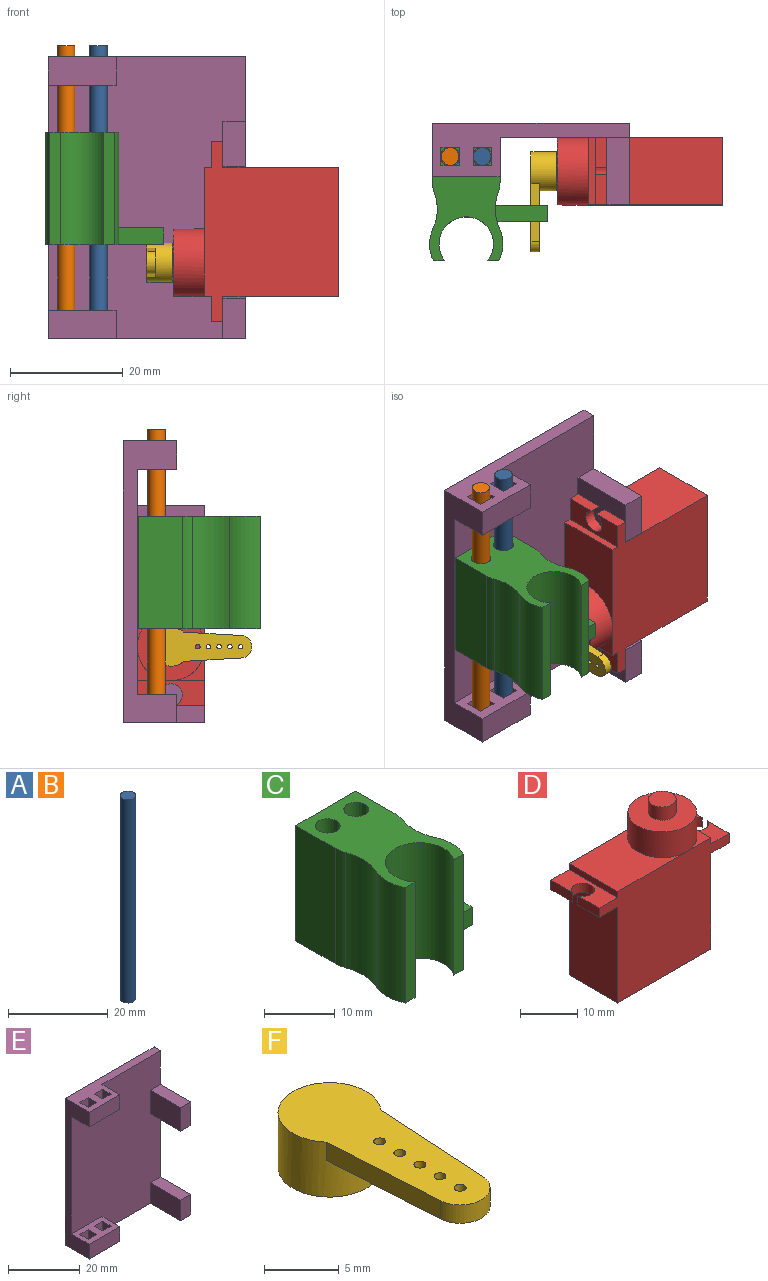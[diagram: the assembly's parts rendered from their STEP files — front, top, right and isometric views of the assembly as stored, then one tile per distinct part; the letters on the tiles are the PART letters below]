
ASSEMBLY  parts=6 mates=5
PART A: 3 faces, bbox 3.1x3.1x50 mm
  f0: cylinder r=1.55mm len=50mm, axis (0,0,-1), area 486.9mm2, adj f1,f2
  f1: plane 3.1x3.1mm, normal (0,0,1), area 7.5mm2, adj f0
  f2: plane 3.1x3.1mm, normal (0,0,-1), area 7.5mm2, adj f0
PART B: same geometry as A
PART C: 20 faces, bbox 21x21.7x20 mm
  f0: cylinder r=6.5mm len=20mm, axis (0,0,-1), area 116.8mm2, adj f1,f12,f14,f15
  f1: plane 20x1.94mm, normal (0,-1,0), area 38.8mm2, adj f0,f2,f14,f15
  f2: cylinder r=4.85mm len=20mm, axis (0,0,-1), area 431.5mm2, adj f1,f3,f14,f15
  f3: plane 20x1.94mm, normal (0,-1,0), area 38.8mm2, adj f2,f4,f14,f15
  f4: cylinder r=6.5mm len=20mm, axis (0,0,-1), area 116.8mm2, adj f3,f5,f14,f15
  f5: cylinder r=8.5mm len=20mm, axis (0,0,-1), area 124.3mm2, adj f4,f6,f14,f15,f16,f18,f19
  f6: cylinder r=5mm len=20mm, axis (0,0,-1), area 35.7mm2, adj f5,f7,f14,f15
  f7: plane 20x7.86mm, normal (1,0,0), area 157.2mm2, adj f6,f8,f14,f15
  f8: plane 20x12mm, normal (0,1,0), area 240mm2, adj f7,f9,f14,f15
  f9: plane 20x7.86mm, normal (-1,0,0), area 157.2mm2, adj f8,f10,f14,f15
  f10: cylinder r=5mm len=20mm, axis (0,0,-1), area 35.7mm2, adj f9,f12,f14,f15
  f11: cylinder r=1.75mm len=20mm, axis (0,0,-1), area 219.9mm2, adj f14,f15
  f12: cylinder r=8.5mm len=20mm, axis (0,0,-1), area 133.3mm2, adj f0,f10,f14,f15
  f13: cylinder r=1.75mm len=20mm, axis (0,0,-1), area 219.9mm2, adj f14,f15
  f14: plane 21.74x13mm, normal (0,0,1), area 172.7mm2, adj f0,f1,f2,f3,f4,f5,f6,f7
  f15: plane 21.74x21mm, normal (0,0,-1), area 200.5mm2, adj f0,f1,f2,f3,f4,f5,f6,f7
  f16: plane 9.05x3mm, normal (0,-1,0), area 27.1mm2, adj f5,f15,f17,f18
  f17: plane 3x3mm, normal (1,0,0), area 9mm2, adj f15,f16,f18,f19
  f18: plane 9.35x3mm, normal (0,0,1), area 27.8mm2, adj f5,f16,f17,f19
  f19: plane 9.32x3mm, normal (0,1,0), area 27.9mm2, adj f5,f15,f17,f18
PART D: 24 faces, bbox 32x12x32.1 mm
  f0: plane 6x6mm, normal (0,0,1), area 7.7mm2, adj f3,f4,f20
  f1: plane 17x12mm, normal (0,0,1), area 147.5mm2, adj f2,f4,f6,f20
  f2: plane 12x1.3mm, normal (-1,0,0), area 15.6mm2, adj f1,f4,f6,f18
  f3: plane 12x1.3mm, normal (1,0,0), area 15.6mm2, adj f0,f4,f6,f9,f13
  f4: plane 32x23.8mm, normal (0,-1,0), area 565.4mm2, adj f0,f1,f2,f3,f5,f7,f8,f10
  f5: plane 20.5x12mm, normal (1,0,0), area 246mm2, adj f4,f6,f8,f14
  f6: plane 32x23.8mm, normal (0,1,0), area 565.4mm2, adj f1,f2,f3,f5,f7,f8,f9,f12
  f7: plane 20.5x12mm, normal (-1,0,0), area 246mm2, adj f4,f6,f8,f19
  f8: plane 23x12mm, normal (0,0,-1), area 276mm2, adj f4,f5,f6,f7
  f9: plane 6x6mm, normal (0,0,1), area 7.7mm2, adj f3,f6,f20
  f10: plane 5.38x2mm, normal (1,0,0), area 10.8mm2, adj f4,f11,f13,f14
  f11: cylinder r=2mm len=4mm, axis (0,0,-1), area 22.6mm2, adj f10,f12,f13,f14
  f12: plane 5.38x2mm, normal (1,0,0), area 10.8mm2, adj f6,f11,f13,f14
  f13: plane 12x4.5mm, normal (0,0,1), area 41.5mm2, adj f3,f4,f6,f10,f11,f12
  f14: plane 12x4.5mm, normal (0,0,-1), area 41.5mm2, adj f4,f5,f6,f10,f11,f12
  f15: plane 5.38x2mm, normal (-1,0,0), area 10.8mm2, adj f6,f16,f18,f19
  f16: cylinder r=2mm len=4mm, axis (0,0,-1), area 22.6mm2, adj f15,f17,f18,f19
  f17: plane 5.38x2mm, normal (-1,0,0), area 10.8mm2, adj f4,f16,f18,f19
  f18: plane 12x4.5mm, normal (0,0,1), area 41.5mm2, adj f2,f4,f6,f15,f16,f17
  f19: plane 12x4.5mm, normal (0,0,-1), area 41.5mm2, adj f4,f6,f7,f15,f16,f17
  f20: cylinder r=6mm len=12mm, axis (0,0,-1), area 207.3mm2, adj f0,f1,f9,f21
  f21: plane 12x12mm, normal (0,0,1), area 94.6mm2, adj f20,f22
  f22: cylinder r=2.43mm len=4.85mm, axis (0,0,-1), area 42.7mm2, adj f21,f23
  f23: plane 4.85x4.85mm, normal (0,0,1), area 18.5mm2, adj f22
PART E: 37 faces, bbox 35x14.5x50 mm
  f0: plane 50x35mm, normal (0,-1,0), area 1570mm2, adj f7,f8,f9,f10,f13,f22,f25,f27
  f1: plane 3.3x3mm, normal (0,-1,0), area 9.9mm2, adj f2,f4,f27,f29
  f2: plane 3.3x3mm, normal (1,0,0), area 9.9mm2, adj f1,f3,f27,f29
  f3: plane 3.3x3mm, normal (0,1,0), area 9.9mm2, adj f2,f4,f27,f29
  f4: plane 3.3x3mm, normal (-1,0,0), area 9.9mm2, adj f1,f3,f27,f29
  f5: plane 3.3x3mm, normal (0,1,0), area 9.9mm2, adj f23,f26,f27,f28
  f6: plane 3.3x3mm, normal (0,-1,0), area 9.9mm2, adj f23,f26,f27,f28
  f7: plane 50x9.5mm, normal (-1,0,0), area 195mm2, adj f0,f8,f10,f11,f12,f22,f24,f27
  f8: plane 35x14.5mm, normal (0,0,-1), area 219.5mm2, adj f0,f7,f9,f11,f24,f25,f31,f32
  f9: plane 50x14.5mm, normal (1,0,0), area 305mm2, adj f0,f8,f10,f11,f30,f32,f33,f35
  f10: plane 35x9.5mm, normal (0,0,1), area 149.7mm2, adj f0,f7,f9,f11,f12,f13,f14,f15
  f11: plane 50x35mm, normal (0,1,0), area 1750mm2, adj f7,f8,f9,f10
  f12: plane 12x5mm, normal (0,-1,0), area 60mm2, adj f7,f10,f13,f22
  f13: plane 7x5mm, normal (1,0,0), area 35mm2, adj f0,f10,f12,f22
  f14: plane 5x3.3mm, normal (0,1,0), area 16.5mm2, adj f10,f15,f20,f22
  f15: plane 5x3.3mm, normal (1,0,0), area 16.5mm2, adj f10,f14,f16,f22
  f16: plane 5x3.3mm, normal (0,-1,0), area 16.5mm2, adj f10,f15,f20,f22
  f17: plane 5x3.3mm, normal (0,-1,0), area 16.5mm2, adj f10,f18,f21,f22
  f18: plane 5x3.3mm, normal (-1,0,0), area 16.5mm2, adj f10,f17,f19,f22
  f19: plane 5x3.3mm, normal (0,1,0), area 16.5mm2, adj f10,f18,f21,f22
  f20: plane 5x3.3mm, normal (-1,0,0), area 16.5mm2, adj f10,f14,f16,f22
  f21: plane 5x3.3mm, normal (1,0,0), area 16.5mm2, adj f10,f17,f19,f22
  f22: plane 12x7mm, normal (0,0,-1), area 62.2mm2, adj f0,f7,f12,f13,f14,f15,f16,f17
  f23: plane 3.3x3mm, normal (-1,0,0), area 9.9mm2, adj f5,f6,f27,f28
  f24: plane 12x5mm, normal (0,-1,0), area 60mm2, adj f7,f8,f25,f27
  f25: plane 7x5mm, normal (1,0,0), area 35mm2, adj f0,f8,f24,f27
  f26: plane 3.3x3mm, normal (1,0,0), area 9.9mm2, adj f5,f6,f27,f28
  f27: plane 12x7mm, normal (0,0,1), area 62.2mm2, adj f0,f1,f2,f3,f4,f5,f6,f7
  f28: plane 3.3x3.3mm, normal (0,0,1), area 10.9mm2, adj f5,f6,f23,f26
  f29: plane 3.3x3.3mm, normal (0,0,1), area 10.9mm2, adj f1,f2,f3,f4
  f30: plane 12x4mm, normal (0,0,1), area 48mm2, adj f0,f9,f31,f32
  f31: plane 12x7mm, normal (-1,0,0), area 84mm2, adj f0,f8,f30,f32
  f32: plane 7x4mm, normal (0,-1,0), area 28mm2, adj f8,f9,f30,f31
  f33: plane 12x4mm, normal (0,0,1), area 48mm2, adj f0,f9,f34,f36
  f34: plane 12x8mm, normal (-1,0,0), area 96mm2, adj f0,f33,f35,f36
  f35: plane 12x4mm, normal (0,0,-1), area 48mm2, adj f0,f9,f34,f36
  f36: plane 8x4mm, normal (0,-1,0), area 32mm2, adj f9,f33,f34,f35
PART F: 14 faces, bbox 6.9x17.8x4.5 mm
  f0: cylinder r=2.43mm len=4.85mm, axis (0,0,1), area 39.6mm2, adj f2,f3
  f1: cylinder r=3.45mm len=6.9mm, axis (0,0,1), area 88.7mm2, adj f2,f4,f5,f12,f13
  f2: plane 6.9x6.9mm, normal (0,0,-1), area 18.9mm2, adj f0,f1
  f3: plane 4.85x4.85mm, normal (0,0,-1), area 18.5mm2, adj f0
  f4: plane 17.8x6.9mm, normal (0,0,1), area 83.3mm2, adj f1,f5,f6,f7,f8,f9,f10,f11
  f5: plane 10.2x1.5mm, normal (-1,-0.06,0), area 15.3mm2, adj f1,f4,f6,f13
  f6: cylinder r=2mm len=3.99mm, axis (0,0,-1), area 9.1mm2, adj f4,f5,f12,f13
  f7: cylinder r=0.4mm len=1.5mm, axis (0,0,-1), area 3.8mm2, adj f4,f13
  f8: cylinder r=0.4mm len=1.5mm, axis (0,0,-1), area 3.8mm2, adj f4,f13
  f9: cylinder r=0.4mm len=1.5mm, axis (0,0,-1), area 3.8mm2, adj f4,f13
  f10: cylinder r=0.4mm len=1.5mm, axis (0,0,-1), area 3.8mm2, adj f4,f13
  f11: cylinder r=0.4mm len=1.5mm, axis (0,0,-1), area 3.8mm2, adj f4,f13
  f12: plane 10.2x1.5mm, normal (1,-0.06,0), area 15.3mm2, adj f1,f4,f6,f13
  f13: plane 12.08x5.2mm, normal (0,0,-1), area 45.9mm2, adj f1,f5,f6,f7,f8,f9,f10,f11
PLACE A rot(axis=(-0.05,0.98,0.18),0deg) t=(69.8,8.32,9.22)mm
PLACE B rot(axis=(-0.05,0.98,0.18),0deg) t=(64.1,8.32,9.22)mm
PLACE C rot(axis=(-0.05,0.98,0.18),0deg) t=(33.02,-23.64,23.87)mm
PLACE D rot(axis=(0.71,0,-0.71),180deg) t=(47.32,-14.44,20.65)mm
PLACE E rot(axis=(-0.05,0.98,0.18),0deg) t=(62.81,-5.94,68.1)mm
PLACE F rot(axis=(0,-1,0),90deg) t=(47.32,-14.44,20.65)mm
MATE fastened E.f29 <-> B.f0  axis (0,0,1) through (19.47,-11.89,9.22)mm
MATE revolute F.f0 <-> D.f20  axis (-1,0,0) through (35.72,-14.44,20.65)mm
MATE fastened D.f16 <-> E.f34  axis (1,0,0) through (47.32,-14.44,40.25)mm
MATE slider C.f11 <-> B.f0  axis (0,0,1) through (19.47,-11.89,43.87)mm
MATE fastened E.f28 <-> A.f0  axis (0,0,1) through (25.17,-11.89,9.22)mm
